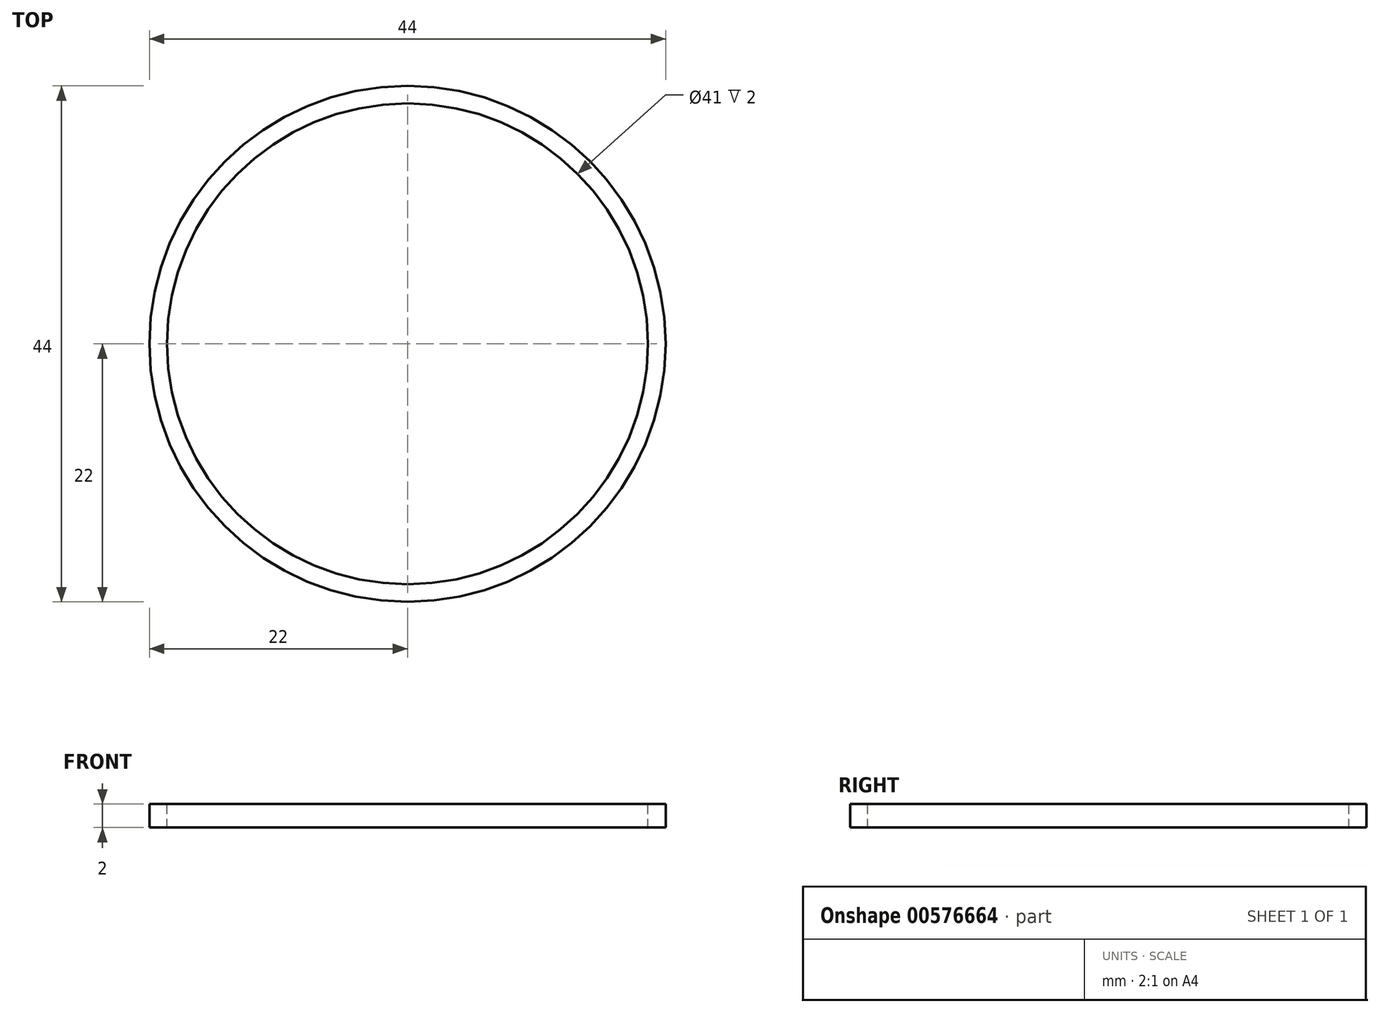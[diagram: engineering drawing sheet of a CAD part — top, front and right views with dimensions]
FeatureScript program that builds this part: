
annotation { "Feature Type Name" : "Feature", "Feature Type Description" : "" }
export const myFeature = defineFeature(function(context is Context, id is Id, definition is map)
    precondition{}
    {
        {
            var Q0;
            Q0=qCreatedBy(makeId("Top.planeOp"),FACE);
            var sketch = newSketch(context, id + "F0", { "sketchPlane" : qUnion([Q0])});
            skCircle(sketch, "E0", {"center": v(0, 0) * mm, "radius": 22 * mm});
            skSolve(sketch);
        }
        {
            var Q0;
            Q0=makeQuery(id+"F0.imprint","IMPRINT",FACE,{"disambiguationData":[TD([[makeQuery(id+"F0.imprint","IMPRINT",EDGE,{"derivedFrom":sQuery(id+"F0.wireOp",EDGE,"E0")}),1.0]])]});
            extrude(context, id + "F1", {"entities" : qUnion([Q0]), "depth" : 2 * mm, "offsetDistance" : 25 * mm});
        }
        {
            var Q0;
            Q0=makeQuery(id+"F1.opExtrude","CAP_FACE",FACE,{"disambiguationData":[OSD([sQuery(id+"F0.wireOp",EDGE,"E0")])],"isStart":false});
            var sketch = newSketch(context, id + "F2", { "sketchPlane" : qUnion([Q0])});
            skCircle(sketch, "E1", {"center": v(0, 0) * mm, "radius": 22 * mm});
            skSolve(sketch);
        }
        {
            var Q0;
            Q0=sQuery(id+"F2.wireOp",VERTEX,"E1.center");
            var Q1;
            Q1=makeQuery(id+"F1.opExtrude","SWEPT_BODY",BODY,{"disambiguationData":[OSD([sQuery(id+"F0.wireOp",EDGE,"E0")])]});
            hole(context, id + "F3", {"style" : HoleStyle.SIMPLE, "endStyle" : HoleEndStyle.BLIND, "holeDiameter" : 41 * mm, "majorDiameter" : 5 * mm, "holeDepth" : 2 * mm, "isTappedThrough" : true, "tappedDepth" : 12 * mm, "tapClearance" : 3, "startFromSketch" : true, "locations" : qUnion([Q0]), "scope" : qUnion([Q1])});
        }
    });
